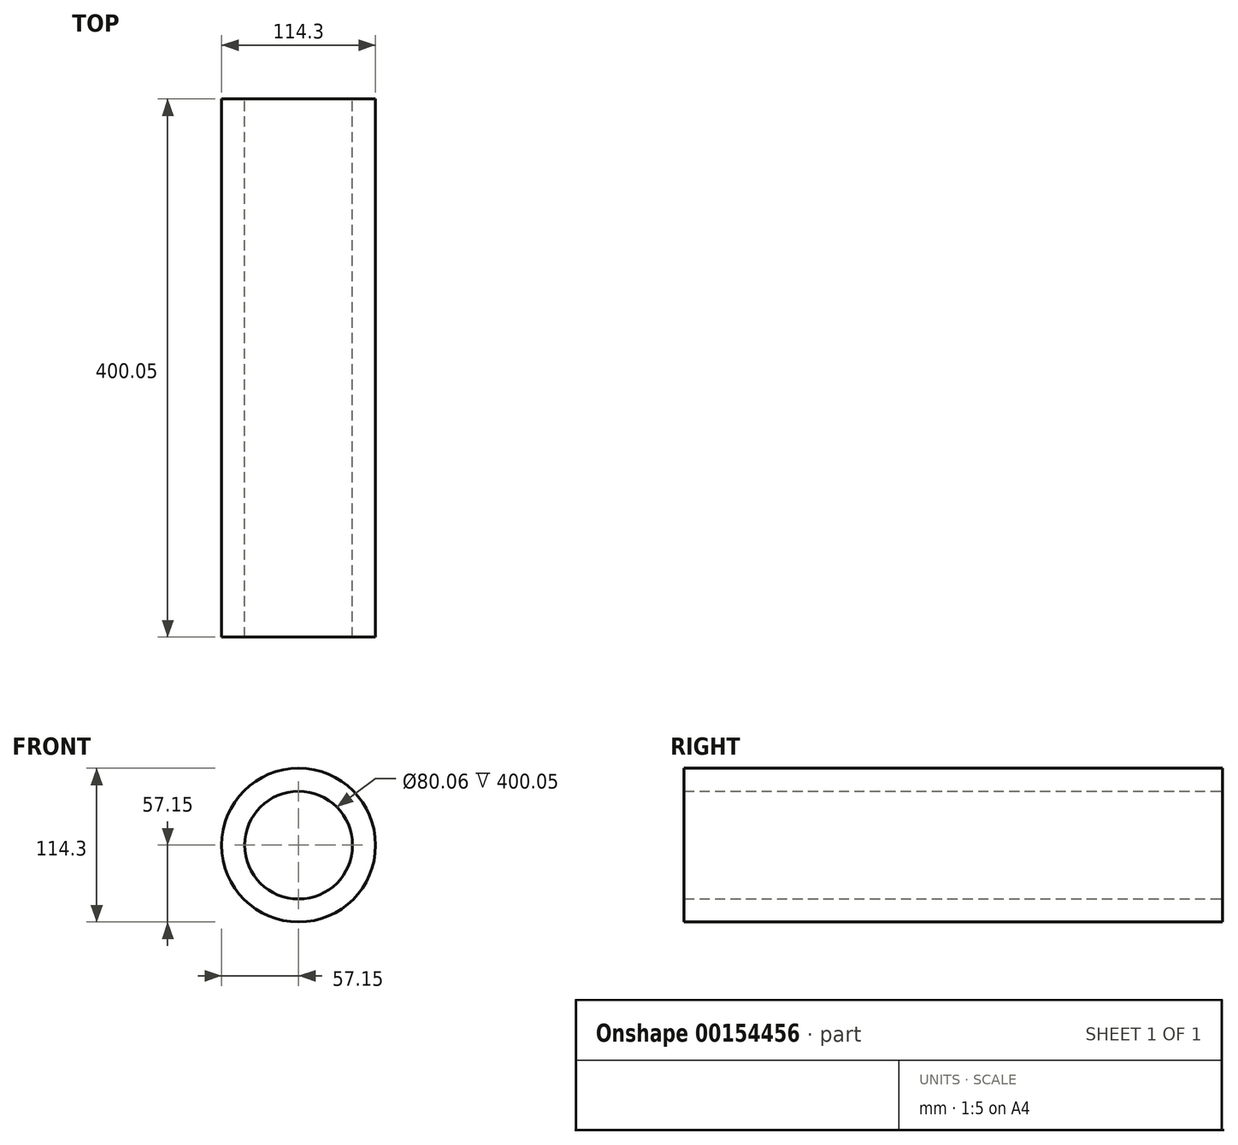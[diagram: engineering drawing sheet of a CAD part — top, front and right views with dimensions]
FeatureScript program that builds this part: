
annotation { "Feature Type Name" : "Feature", "Feature Type Description" : "" }
export const myFeature = defineFeature(function(context is Context, id is Id, definition is map)
    precondition{}
    {
        {
            var Q0;
            Q0=qCreatedBy(makeId("Front.planeOp"),FACE);
            var sketch = newSketch(context, id + "F0", { "sketchPlane" : qUnion([Q0])});
            skCircle(sketch, "E0", {"center": v(0, 0) * mm, "radius": 57.15 * mm});
            skCircle(sketch, "E1.0", {"center": v(0, 0) * mm, "radius": 40.03 * mm});
            skSolve(sketch);
        }
        {
            var Q0;
            Q0=makeQuery(id+"F0.imprint","IMPRINT",FACE,{"disambiguationData":[TD([[makeQuery(id+"F0.imprint","IMPRINT",EDGE,{"derivedFrom":sQuery(id+"F0.wireOp",EDGE,"E0")}),1.0]])]});
            extrude(context, id + "F1", {"entities" : qUnion([Q0]), "depth" : 400.05 * mm});
        }
    });
